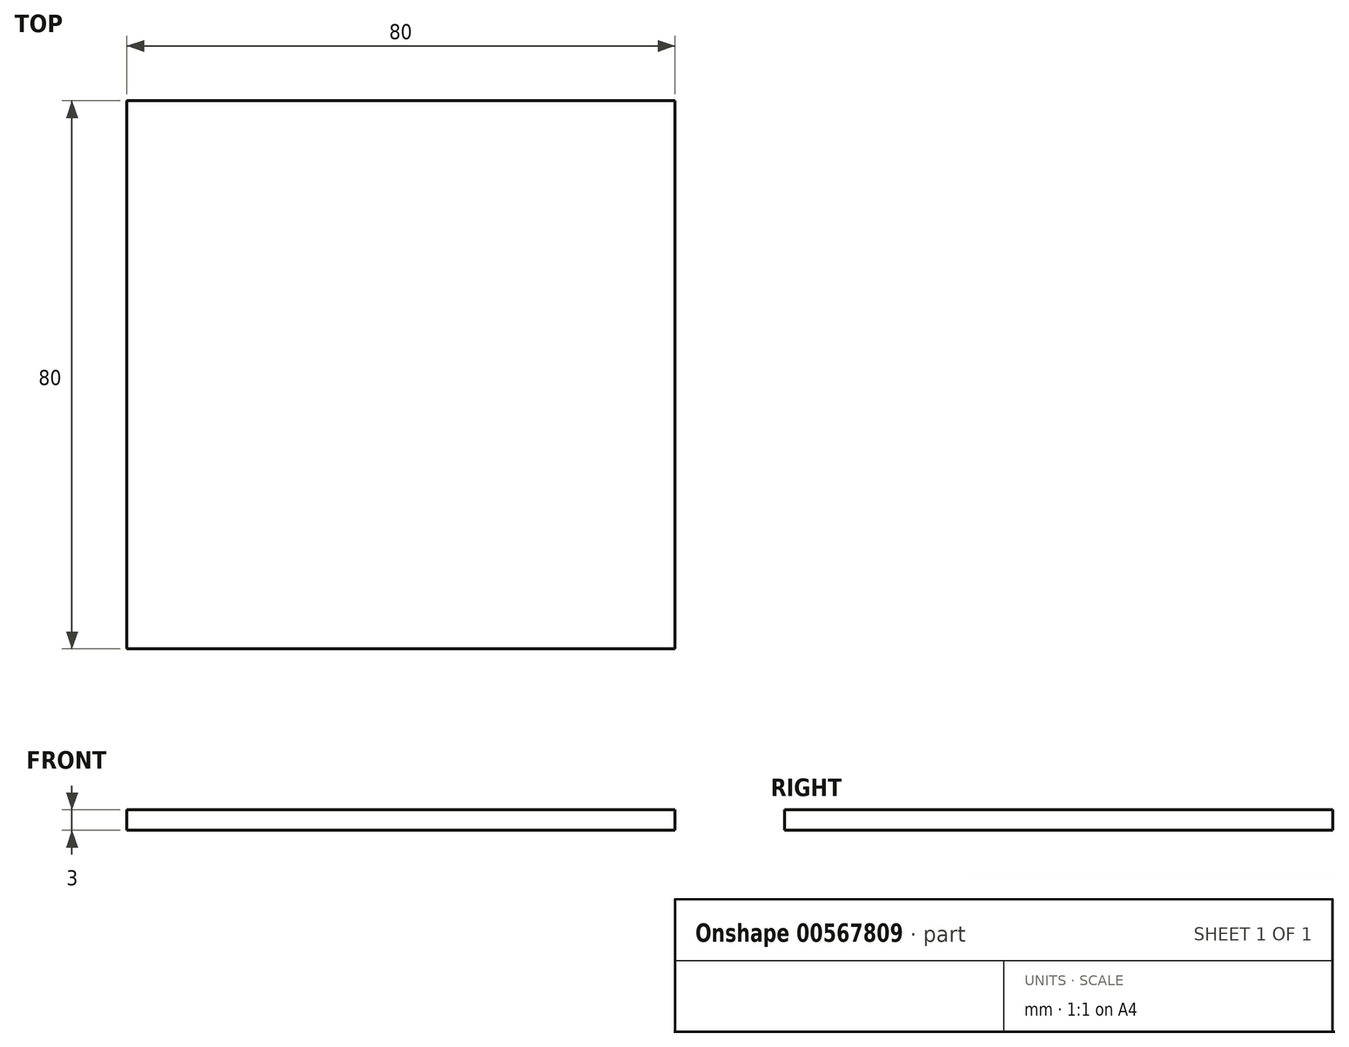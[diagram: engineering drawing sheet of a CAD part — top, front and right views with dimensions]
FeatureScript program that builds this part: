
annotation { "Feature Type Name" : "Feature", "Feature Type Description" : "" }
export const myFeature = defineFeature(function(context is Context, id is Id, definition is map)
    precondition{}
    {
        {
            var Q0;
            Q0=qCreatedBy(makeId("Top.planeOp"),FACE);
            var sketch = newSketch(context, id + "F0", { "sketchPlane" : qUnion([Q0])});
            skLineSegment(sketch, "E0.bottom", {"start": v(-40, 40) * mm, "end": v(40, 40) * mm});
            skLineSegment(sketch, "E0.top", {"start": v(-40, -40) * mm, "end": v(40, -40) * mm});
            skLineSegment(sketch, "E0.left", {"start": v(-40, 40) * mm, "end": v(-40, -40) * mm});
            skLineSegment(sketch, "E0.right", {"start": v(40, 40) * mm, "end": v(40, -40) * mm});
            skPoint(sketch, "E0.middle", {"position": v(0, 0) * mm});
            skSolve(sketch);
        }
        {
            var Q0;
            Q0=makeQuery(id+"F0.imprint","IMPRINT",FACE,{"disambiguationData":[TD([[makeQuery(id+"F0.imprint","IMPRINT",EDGE,{"derivedFrom":sQuery(id+"F0.wireOp",EDGE,"E0.bottom")}),-1.0]])]});
            extrude(context, id + "F1", {"entities" : qUnion([Q0]), "depth" : 3 * mm, "offsetDistance" : 25 * mm});
        }
    });
